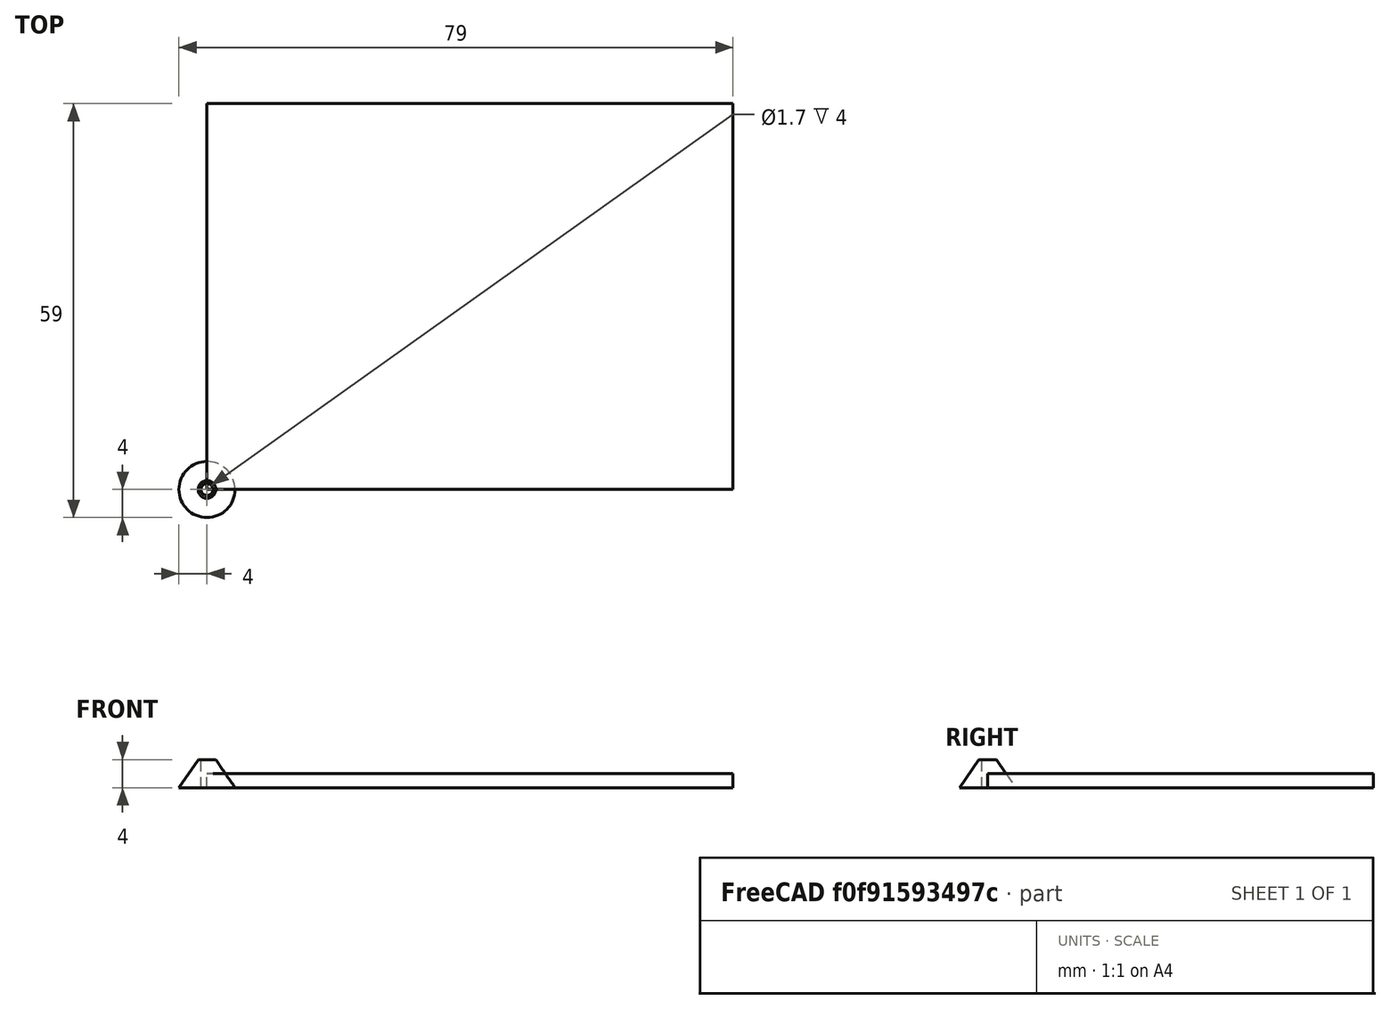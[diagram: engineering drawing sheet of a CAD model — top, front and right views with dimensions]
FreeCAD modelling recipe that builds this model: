
FCSTD DOCUMENT  (FreeCAD 1.0R39319 (Git))
Label: perfboard-standoffs
License: All rights reserved
LicenseURL: https://en.wikipedia.org/wiki/All_rights_reserved
objects: App::Link×8, Sketcher::SketchObject×4, PartDesign::Body×2, Assembly::JointGroup×2, Assembly::AssemblyObject×2, PartDesign::Plane×1, PartDesign::AdditiveLoft×1, PartDesign::Pocket×1, App::FeaturePython×1, Assembly::AssemblyLink×1, PartDesign::Pad×1
note: 20 computed .brp shape members not serialized (recipe doc carries the construction recipe); baked Part::Feature solids carry a one-line shape summary decoded from their .brp

FEATURE [Sketcher::SketchObject] Sketch
  ArcFitTolerance = 1e-06
  AttachmentSupport = -> [XY_Plane001]
  FullyConstrained = true
  MakeInternals = false
  MapMode = 5
  sketch-geometry (1):
    g0: Circle CenterX=0 CenterY=0 CenterZ=0 NormalX=0 NormalY=0 NormalZ=1 AngleXU=0 Radius=4
  constraints (2):
    c: Diameter(g0) = 8
    c: Coincident(g0,g-1)
FEATURE [PartDesign::Plane] DatumPlane
  AttachmentOffset = pos=(0,0,4) rot=(0,0,1;0rad)
  AttachmentSupport = -> [Sketch]
  Length = 60
  MapMode = 2
  Placement = pos=(0,0,4) rot=(0,0,1;0rad)
  ResizeMode = 0
  Width = 60
FEATURE [Sketcher::SketchObject] Sketch001
  ArcFitTolerance = 1e-06
  AttachmentSupport = -> [DatumPlane]
  FullyConstrained = true
  MakeInternals = false
  MapMode = 5
  Placement = pos=(0,0,4) rot=(0,0,1;0rad)
  sketch-geometry (1):
    g0: Circle CenterX=0 CenterY=0 CenterZ=0 NormalX=0 NormalY=0 NormalZ=1 AngleXU=0 Radius=1.25
  constraints (2):
    c: Diameter(g0) = 2.5
    c: Coincident(g0,g-1)
FEATURE [PartDesign::AdditiveLoft] AdditiveLoft
  Closed = false
  Placement = pos=(0,0,4) rot=(0,0,1;0rad)
  Profile = -> Sketch001
  Refine = true
  Ruled = false
  Sections = -> [Sketch]
  Suppressed = false
FEATURE [Sketcher::SketchObject] Sketch002
  ArcFitTolerance = 1e-06
  AttachmentSupport = -> [AdditiveLoft]
  FullyConstrained = true
  MakeInternals = false
  MapMode = 5
  Placement = pos=(0,0,4) rot=(0,0,1;0rad)
  sketch-geometry (1):
    g0: Circle CenterX=0 CenterY=0 CenterZ=0 NormalX=0 NormalY=0 NormalZ=1 AngleXU=0 Radius=0.85
  constraints (2):
    c: Diameter(g0) = 1.7
    c: Coincident(g0,g-1)
FEATURE [PartDesign::Pocket] Pocket
  BaseFeature = -> AdditiveLoft
  Direction = (0,0,-1)
  Length = 5
  Length2 = 5
  Placement = pos=(0,0,4) rot=(0,0,1;0rad)
  Profile = -> Sketch002
  ReferenceAxis = -> Sketch002 [N_Axis]
  Refine = true
  Suppressed = false
  Type = 0
FEATURE [PartDesign::Body] Body  label="standoff"
  AllowCompound = false
  Group = -> [Sketch,DatumPlane,Sketch001,AdditiveLoft,Sketch002,Pocket]
  Origin = -> Origin001
  Tip = -> Pocket
FEATURE [App::Link] standoff  label="standoff001"
  LinkedObject = -> Body
FEATURE [App::FeaturePython] GroundedJoint  # Assembly grounded joint (typed FeaturePython)
  ObjectToGround = -> standoff
FEATURE [Assembly::JointGroup] Joints
  Group = -> [GroundedJoint]
FEATURE [App::Link] standoff001  label="standoff002"
  LinkPlacement = pos=(64.8,0,0) rot=(0,0,1;0rad)
  LinkedObject = -> Body
  Placement = pos=(64.8,0,0) rot=(0,0,1;0rad)
FEATURE [App::Link] standoff002  label="standoff003"
  LinkPlacement = pos=(0,45,0) rot=(0,0,1;0rad)
  LinkedObject = -> Body
  Placement = pos=(0,45,0) rot=(0,0,1;0rad)
FEATURE [App::Link] standoff003  label="standoff004"
  LinkPlacement = pos=(64.8,45,0) rot=(0,0,1;0rad)
  LinkedObject = -> Body
  Placement = pos=(64.8,45,0) rot=(0,0,1;0rad)
FEATURE [Assembly::AssemblyObject] Assembly  label="standoffs"
  Group = -> [Joints,standoff,GroundedJoint,standoff001,standoff002,standoff003]
  Origin = -> Origin
  Type = Assembly
FEATURE [Assembly::JointGroup] Joints001
FEATURE [App::Link] standoff004  label="standoff005"
  LinkedObject = -> standoff
FEATURE [App::Link] standoff005  label="standoff006"
  LinkPlacement = pos=(64.8,0,0) rot=(0,0,1;0rad)
  LinkedObject = -> standoff001
  Placement = pos=(64.8,0,0) rot=(0,0,1;0rad)
FEATURE [App::Link] standoff006  label="standoff007"
  LinkPlacement = pos=(0,45,0) rot=(0,0,1;0rad)
  LinkedObject = -> standoff002
  Placement = pos=(0,45,0) rot=(0,0,1;0rad)
FEATURE [App::Link] standoff007  label="standoff008"
  LinkPlacement = pos=(64.8,45,0) rot=(0,0,1;0rad)
  LinkedObject = -> standoff003
  Placement = pos=(64.8,45,0) rot=(0,0,1;0rad)
FEATURE [Assembly::AssemblyLink] standoffs  label="standoffs001"
  Group = -> [standoff004,standoff005,standoff006,standoff007]
  LinkedObject = -> Assembly
  Origin = -> Origin003
  Placement = pos=(5,6,2) rot=(0,0,1;0rad)
  Rigid = true
FEATURE [Sketcher::SketchObject] Sketch003
  ArcFitTolerance = 1e-06
  AttachmentSupport = -> [XY_Plane005]
  FullyConstrained = true
  MakeInternals = false
  MapMode = 5
  sketch-geometry (4):
    g0: LineSegment StartX=0 StartY=0 StartZ=0 EndX=75 EndY=0 EndZ=0
    g1: LineSegment StartX=75 StartY=0 StartZ=0 EndX=75 EndY=55 EndZ=0
    g2: LineSegment StartX=75 StartY=55 StartZ=0 EndX=0 EndY=55 EndZ=0
    g3: LineSegment StartX=0 StartY=55 StartZ=0 EndX=0 EndY=0 EndZ=0
  constraints (11):
    c: Coincident(g0,g1)
    c: Coincident(g1,g2)
    c: Coincident(g2,g3)
    c: Coincident(g3,g0)
    c: Horizontal(g0)
    c: Horizontal(g2)
    c: Vertical(g1)
    c: Vertical(g3)
    c: Distance(g1,g3) = 75
    c: Distance(g0,g2) = 55
    c: Coincident(g0,g-1)
FEATURE [PartDesign::Pad] Pad
  Direction = (0,0,1)
  Length = 2
  Length2 = 10
  Profile = -> Sketch003
  ReferenceAxis = -> Sketch003 [N_Axis]
  Refine = true
  Suppressed = false
  Type = 0
FEATURE [PartDesign::Body] Body001  label="Body"
  AllowCompound = false
  Group = -> [Sketch003,Pad]
  Origin = -> Origin005
  Tip = -> Pad
FEATURE [Assembly::AssemblyObject] Assembly001  label="print-test"
  Group = -> [Joints001,standoffs,Body001]
  Origin = -> Origin002
  Type = Assembly
